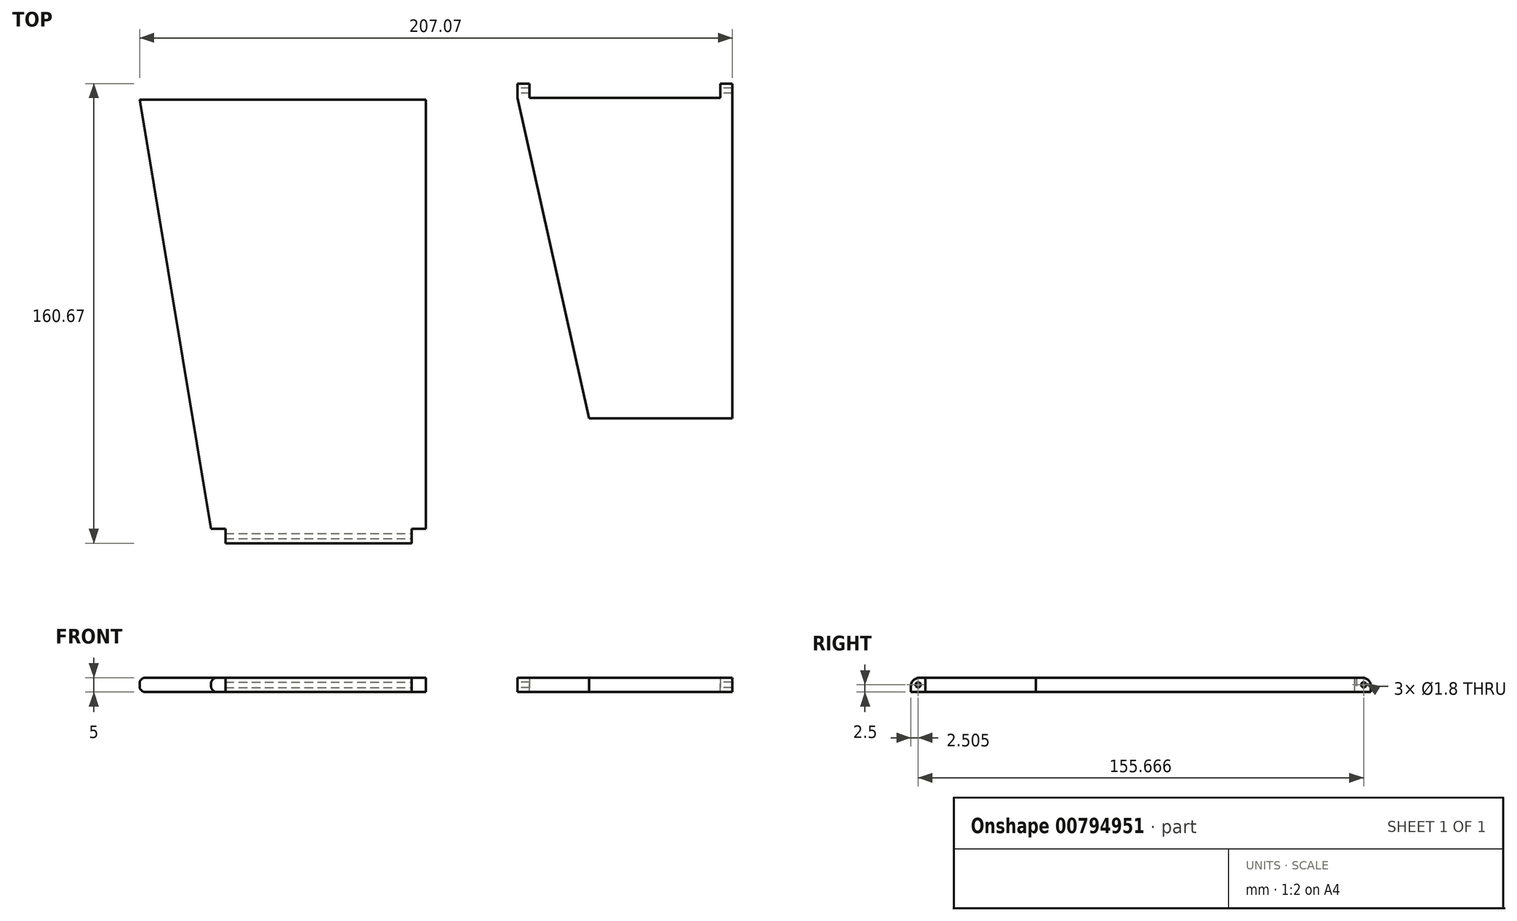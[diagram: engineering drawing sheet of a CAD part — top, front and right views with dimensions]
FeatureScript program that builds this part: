
annotation { "Feature Type Name" : "Feature", "Feature Type Description" : "" }
export const myFeature = defineFeature(function(context is Context, id is Id, definition is map)
    precondition{}
    {
        {
            var Q0;
            Q0=qCreatedBy(makeId("Top.planeOp"),FACE);
            var sketch = newSketch(context, id + "F0", { "sketchPlane" : qUnion([Q0])});
            skLineSegment(sketch, "E0.top", {"start": v(45.68, -36) * mm, "end": v(95.68, -36) * mm});
            skLineSegment(sketch, "E1", {"start": v(70.68, -36) * mm, "end": v(70.68, 114) * mm});
            skLineSegment(sketch, "E2", {"start": v(95.68, 76) * mm, "end": v(95.68, -36) * mm});
            skLineSegment(sketch, "E3", {"start": v(20.68, 76) * mm, "end": v(45.68, -36) * mm});
            skLineSegment(sketch, "E4", {"start": v(20.68, 76) * mm, "end": v(95.68, 76) * mm});
            skSolve(sketch);
        }
        {
            var Q0;
            Q0 = qSketchRegion(id + "F0", true);
            extrude(context, id + "F1", {"entities" : qUnion([Q0]), "depth" : 5 * mm, "offsetDistance" : 25 * mm});
        }
        {
            var Q0;
            Q0=qCreatedBy(makeId("Top.planeOp"),FACE);
            var sketch = newSketch(context, id + "F2", { "sketchPlane" : qUnion([Q0])});
            skLineSegment(sketch, "E5.bottom", {"start": v(-111.4, 75.33) * mm, "end": v(-11.4, 75.33) * mm});
            skLineSegment(sketch, "E5.right", {"start": v(-11.4, 75.33) * mm, "end": v(-11.4, -74.67) * mm});
            skLineSegment(sketch, "E6", {"start": v(-111.4, 75.33) * mm, "end": v(-86.4, -74.67) * mm});
            skLineSegment(sketch, "E7", {"start": v(-36.4, -74.67) * mm, "end": v(-36.4, 75.33) * mm});
            skLineSegment(sketch, "E8", {"start": v(-86.4, -74.67) * mm, "end": v(-11.4, -74.67) * mm});
            skSolve(sketch);
        }
        {
            var Q0;
            Q0 = qSketchRegion(id + "F2", true);
            extrude(context, id + "F3", {"entities" : qUnion([Q0]), "depth" : 5 * mm, "offsetDistance" : 25 * mm});
        }
        {
            var Q0;
            Q0=makeQuery(id+"F3.opExtrude","CAP_EDGE",EDGE,{"disambiguationData":[OSD([sQuery(id+"F2.wireOp",EDGE,"E6")])],"isStart":false});
            var Q1;
            Q1=makeQuery(id+"F3.opExtrude","CAP_EDGE",EDGE,{"disambiguationData":[OSD([sQuery(id+"F2.wireOp",EDGE,"E6")])],"isStart":true});
            fillet(context, id + "F4", {"entities" : qUnion([Q0, Q1]), "radius" : 2 * mm, "tangentPropagation" : true, "allowEdgeOverflow" : false});
        }
        {
            var Q0;
            Q0=makeQuery(id+"F1.opExtrude","SWEPT_FACE",FACE,{"disambiguationData":[OSD([sQuery(id+"F0.wireOp",EDGE,"E4")])]});
            var sketch = newSketch(context, id + "F5", { "sketchPlane" : qUnion([Q0])});
            skLineSegment(sketch, "E9.bottom", {"start": v(-95.68, 0) * mm, "end": v(-20.68, 0) * mm});
            skLineSegment(sketch, "E9.top", {"start": v(-95.68, 5) * mm, "end": v(-20.68, 5) * mm});
            skLineSegment(sketch, "E9.left", {"start": v(-95.68, 0) * mm, "end": v(-95.68, 5) * mm});
            skLineSegment(sketch, "E9.right", {"start": v(-20.68, 0) * mm, "end": v(-20.68, 5) * mm});
            skSolve(sketch);
        }
        {
            var Q0;
            Q0 = qSketchRegion(id + "F5", true);
            extrude(context, id + "F6", {"entities" : qUnion([Q0]), "operationType" : NewBodyOperationType.ADD, "depth" : 5 * mm, "offsetDistance" : 25 * mm});
        }
        {
            var Q0;
            Q0=makeQuery(id+"F3.opExtrude","SWEPT_FACE",FACE,{"disambiguationData":[OSD([sQuery(id+"F2.wireOp",EDGE,"E8")])]});
            var sketch = newSketch(context, id + "F7", { "sketchPlane" : qUnion([Q0])});
            skLineSegment(sketch, "E10.bottom", {"start": v(-16.4, 0) * mm, "end": v(-81.4, 0) * mm});
            skLineSegment(sketch, "E10.top", {"start": v(-16.4, 5) * mm, "end": v(-81.4, 5) * mm});
            skLineSegment(sketch, "E10.left", {"start": v(-16.4, 0) * mm, "end": v(-16.4, 5) * mm});
            skLineSegment(sketch, "E10.right", {"start": v(-81.4, 0) * mm, "end": v(-81.4, 5) * mm});
            skSolve(sketch);
        }
        {
            var Q0;
            Q0 = qSketchRegion(id + "F7", true);
            extrude(context, id + "F8", {"entities" : qUnion([Q0]), "operationType" : NewBodyOperationType.ADD, "depth" : 5 * mm, "offsetDistance" : 25 * mm});
        }
        {
            var Q0;
            Q0=makeQuery(id+"F6.opExtrude","CAP_FACE",FACE,{"disambiguationData":[OSD([sQuery(id+"F5.wireOp",EDGE,"E9.bottom"),sQuery(id+"F5.wireOp",EDGE,"E9.top"),sQuery(id+"F5.wireOp",EDGE,"E9.left"),sQuery(id+"F5.wireOp",EDGE,"E9.right")])],"isStart":false});
            var sketch = newSketch(context, id + "F9", { "sketchPlane" : qUnion([Q0])});
            skLineSegment(sketch, "E11.bottom", {"start": v(-24.83, -0.16) * mm, "end": v(-91.53, -0.16) * mm});
            skLineSegment(sketch, "E11.top", {"start": v(-24.83, 7.8) * mm, "end": v(-91.53, 7.8) * mm});
            skLineSegment(sketch, "E11.left", {"start": v(-24.83, -0.16) * mm, "end": v(-24.83, 7.8) * mm});
            skLineSegment(sketch, "E11.right", {"start": v(-91.53, -0.16) * mm, "end": v(-91.53, 7.8) * mm});
            skSolve(sketch);
        }
        {
            var Q0;
            Q0 = qSketchRegion(id + "F9", true);
            extrude(context, id + "F10", {"entities" : qUnion([Q0]), "operationType" : NewBodyOperationType.REMOVE, "oppositeDirection" : true, "depth" : 5 * mm, "offsetDistance" : 25 * mm});
        }
        {
            var Q0;
            Q0=makeQuery(id+"F8.opExtrude","SWEPT_FACE",FACE,{"disambiguationData":[OSD([sQuery(id+"F7.wireOp",EDGE,"E10.left")])]});
            var sketch = newSketch(context, id + "F11", { "sketchPlane" : qUnion([Q0])});
            skCircle(sketch, "E12", {"center": v(-77.17, 2.5) * mm, "radius": 0.9 * mm});
            skPoint(sketch, "E12.centerSnap0", {"position": v(-77.17, 5) * mm});
            skPoint(sketch, "E12.centerSnap1", {"position": v(-79.67, 2.5) * mm});
            skSolve(sketch);
        }
        {
            var Q0;
            Q0 = qSketchRegion(id + "F11", true);
            extrude(context, id + "F12", {"entities" : qUnion([Q0]), "operationType" : NewBodyOperationType.REMOVE, "oppositeDirection" : true, "depth" : 100 * mm, "offsetDistance" : 25 * mm});
        }
        {
            var Q0;
            Q0=makeQuery(id+"F6.opExtrude","SWEPT_FACE",FACE,{"disambiguationData":[OSD([sQuery(id+"F5.wireOp",EDGE,"E9.right")])]});
            var sketch = newSketch(context, id + "F13", { "sketchPlane" : qUnion([Q0])});
            skCircle(sketch, "E13", {"center": v(-78.5, 2.5) * mm, "radius": 0.9 * mm});
            skPoint(sketch, "E13.centerSnap0", {"position": v(-81, 2.5) * mm});
            skPoint(sketch, "E13.centerSnap1", {"position": v(-78.5, 0) * mm});
            skSolve(sketch);
        }
        {
            var Q0;
            Q0 = qSketchRegion(id + "F13", true);
            extrude(context, id + "F14", {"entities" : qUnion([Q0]), "operationType" : NewBodyOperationType.REMOVE, "oppositeDirection" : true, "depth" : 125 * mm, "offsetDistance" : 25 * mm});
        }
        {
            var Q0;
            {var subQ0=sQuery(id+"F5.wireOp",EDGE,"E9.top");var subQ1=sQuery(id+"F5.wireOp",EDGE,"E9.right");Q0=makeQuery(id+"F10.boolean.opBoolean","SPLIT",EDGE,{"disambiguationData":[TD([makeQuery(id+"F6.opExtrude","SWEPT_FACE",FACE,{"disambiguationData":[OSD([subQ1])]})])],"derivedFrom":makeQuery(id+"F6.opExtrude","CAP_EDGE",EDGE,{"disambiguationData":[OSD([subQ0])],"isStart":false})});}
            var Q1;
            {var subQ0=sQuery(id+"F5.wireOp",EDGE,"E9.top");var subQ2=sQuery(id+"F0.wireOp",EDGE,"E2");Q1=makeQuery(id+"F10.boolean.opBoolean","SPLIT",EDGE,{"disambiguationData":[TD([makeQuery(id+"F1.opExtrude","SWEPT_FACE",FACE,{"disambiguationData":[OSD([subQ2])]})])],"derivedFrom":makeQuery(id+"F6.opExtrude","CAP_EDGE",EDGE,{"disambiguationData":[OSD([subQ0])],"isStart":false})});}
            var Q2;
            Q2=makeQuery(id+"F8.opExtrude","CAP_EDGE",EDGE,{"disambiguationData":[OSD([sQuery(id+"F7.wireOp",EDGE,"E10.top")])],"isStart":false});
            fillet(context, id + "F15", {"entities" : qUnion([Q0, Q1, Q2]), "radius" : 3 * mm, "tangentPropagation" : true, "allowEdgeOverflow" : false});
        }
    });
